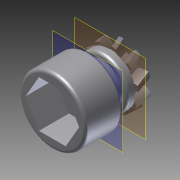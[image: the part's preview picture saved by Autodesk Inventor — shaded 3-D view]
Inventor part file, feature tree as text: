
AUTODESK INVENTOR PART (.ipt)
format: ipt  version: 2012 (Build 160160000, 160)  size: 606,208 bytes
history: native  units: in
note: dims shown in document units (in); Inventor stores cm internally (conversion verified against a paired STEP export)
features: fillet x8, extrude x6, sketch x6, other x3, plane x1
ambient origin geometry x8: Origin, YZ Plane, XZ Plane, XY Plane, X Axis, Y Axis, Z Axis, Center Point
bodies: Solid2 (feature_tree)
feature tree (24):
  other  "SmallOutputGear.iam"
  other  "BlankSmallGearOutput.ipt:1"
  other  "Spur Gear1:1"
  extrude  "Extrusion3"  Depth=0.0276in TaperAngle=0.0deg
  extrude  "Extrusion4"  Depth=0.3937in TaperAngle=0.0deg
  extrude  "Extrusion5"  Depth=0.3937in TaperAngle=0.0deg
  extrude  "Extrusion6"  Depth=0.3937in TaperAngle=0.0deg
  extrude  "Extrusion7"  Depth=0.3937in TaperAngle=0.0deg
  extrude  "Extrusion9"  Depth=0.0591in TaperAngle=0.0deg
  fillet  "Fillet8"  Radius=0.0197in
  fillet  "Fillet9"  Radius=0.0394in
  fillet  "Fillet10"  Radius=0.0394in
  fillet  "Fillet11"  Radius=0.0079in
  fillet  "Fillet12"  Radius=0.0197in
  fillet  "Fillet13"  Radius=0.1181in
  fillet  "Fillet14"  Radius=0.0394in
  fillet  "Fillet15"  Radius=0.0394in
  plane  "Work Plane4"
  sketch  "Sketch5"  dims[d5=0.3937in d6=0.0276in d7=0.0in]
  sketch  "Sketch6"  dims[d8=0.0591in d9=0.3937in d10=0.0in]
  sketch  "Sketch7"  dims[d11=0.0591in d12=0.3937in d13=0.0in]
  sketch  "Sketch8"  dims[d14=0.6299in d15=0.3937in d16=0.0in]
  sketch  "Sketch9"  dims[d17=0.0591in d18=0.3937in d19=0.0in]
  sketch  "Sketch11"  dims[d34=0.0591in d35=0.0591in d36=0.1575in d37=0.0in d38=0.0in d39=0.0197in d40=0.0394in d41=0.0394in d42=0.0079in d43=0.0197in d44=0.1181in d45=0.0394in d46=0.0394in]
